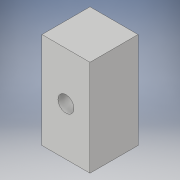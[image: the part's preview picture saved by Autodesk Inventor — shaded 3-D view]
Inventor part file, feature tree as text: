
AUTODESK INVENTOR PART (.ipt)
format: ipt  version: 2018 (Build 220112000, 112)  size: 99,328 bytes
history: native  units: mm
features: sketch x1, extrude x1
ambient origin geometry x8: Origin, YZ Plane, XZ Plane, XY Plane, X Axis, Y Axis, Z Axis, Center Point
bodies: Volumenkörper1 (feature_tree)
feature tree (2):
  sketch  "Skizze1"  dims[d0=30.0mm d1=15.0mm d2=15.0mm d3=7.5mm d4=5.0mm d5=15.0mm d6=0.0mm]
  extrude  "Extrusion1"  Depth=15.0mm
